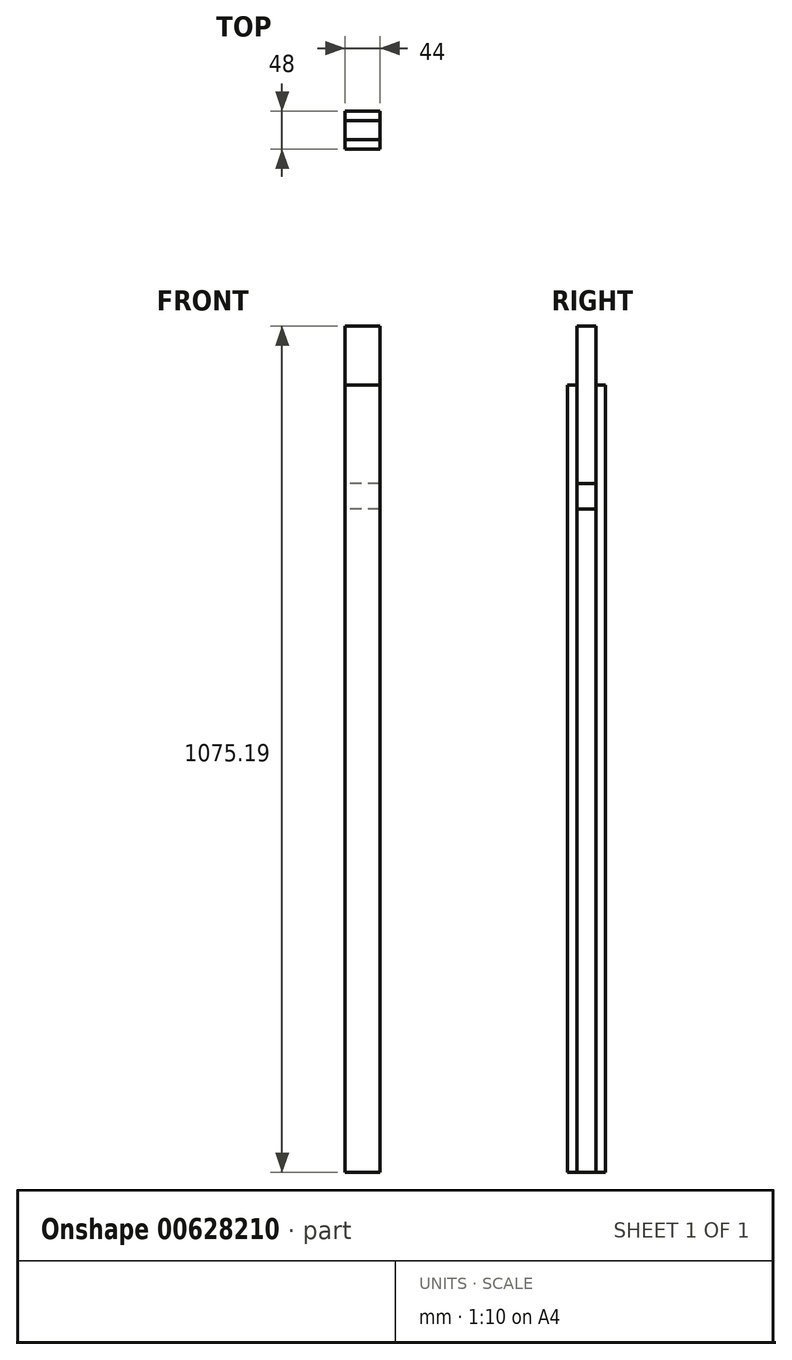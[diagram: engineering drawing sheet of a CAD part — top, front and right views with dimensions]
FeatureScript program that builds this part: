
annotation { "Feature Type Name" : "Feature", "Feature Type Description" : "" }
export const myFeature = defineFeature(function(context is Context, id is Id, definition is map)
    precondition{}
    {
        {
            var Q0;
            Q0=qCreatedBy(makeId("Right.planeOp"),FACE);
            var sketch = newSketch(context, id + "F0", { "sketchPlane" : qUnion([Q0])});
            skLineSegment(sketch, "E0", {"start": v(-12, 0) * mm, "end": v(12, 0) * mm});
            skLineSegment(sketch, "E1", {"start": v(-12, 0) * mm, "end": v(-12, 1000) * mm});
            skLineSegment(sketch, "E2", {"start": v(12, 1000) * mm, "end": v(12, 0) * mm});
            skLineSegment(sketch, "E3", {"start": v(-12, 1000) * mm, "end": v(-24, 1000) * mm});
            skLineSegment(sketch, "E4", {"start": v(-24, 1000) * mm, "end": v(-24, 0) * mm});
            skLineSegment(sketch, "E5", {"start": v(-24, 0) * mm, "end": v(-12, 0) * mm});
            skLineSegment(sketch, "E6", {"start": v(12, 1000) * mm, "end": v(24, 1000) * mm});
            skLineSegment(sketch, "E7", {"start": v(24, 1000) * mm, "end": v(24, 0) * mm});
            skLineSegment(sketch, "E8", {"start": v(24, 0) * mm, "end": v(12, 0) * mm});
            skLineSegment(sketch, "E9", {"start": v(-12, 1000) * mm, "end": v(-12, 1075.19) * mm});
            skLineSegment(sketch, "E10", {"start": v(-12, 1075.19) * mm, "end": v(12, 1075.19) * mm});
            skLineSegment(sketch, "E11", {"start": v(12, 1075.19) * mm, "end": v(12, 1000) * mm});
            skLineSegment(sketch, "E12", {"start": v(-12, 875.19) * mm, "end": v(12, 875.19) * mm});
            skLineSegment(sketch, "E13", {"start": v(-12, 842.84) * mm, "end": v(12, 842.84) * mm});
            skSolve(sketch);
        }
        {
            var Q0;
            {var subQ0=sQuery(id+"F0.wireOp",EDGE,"E3");Q0=makeQuery(id+"F0.imprint","IMPRINT",FACE,{"disambiguationData":[TD([[makeQuery(id+"F0.imprint","IMPRINT",EDGE,{"derivedFrom":subQ0}),1.0]])]});}
            var Q1;
            {var subQ3=sQuery(id+"F0.wireOp",EDGE,"E6");Q1=makeQuery(id+"F0.imprint","IMPRINT",FACE,{"disambiguationData":[TD([[makeQuery(id+"F0.imprint","IMPRINT",EDGE,{"derivedFrom":subQ3}),-1.0]])]});}
            extrude(context, id + "F1", {"entities" : qUnion([Q0, Q1]), "depth" : 44 * mm, "offsetDistance" : 25 * mm});
        }
        {
            var Q0;
            {var subQ0=sQuery(id+"F0.wireOp",EDGE,"E0");Q0=makeQuery(id+"F0.imprint","IMPRINT",FACE,{"disambiguationData":[TD([[makeQuery(id+"F0.imprint","IMPRINT",EDGE,{"derivedFrom":subQ0}),1.0]])]});}
            var Q1;
            {var subQ0=sQuery(id+"F0.wireOp",EDGE,"E9");Q1=makeQuery(id+"F0.imprint","IMPRINT",FACE,{"disambiguationData":[TD([[makeQuery(id+"F0.imprint","IMPRINT",EDGE,{"derivedFrom":subQ0}),-1.0]])]});}
            var Q2;
            Q2=makeQuery(id+"F1.opExtrude","CAP_FACE",FACE,{"disambiguationData":[OSD([sQuery(id+"F0.wireOp",EDGE,"E2"),sQuery(id+"F0.wireOp",EDGE,"E6"),sQuery(id+"F0.wireOp",EDGE,"E7"),sQuery(id+"F0.wireOp",EDGE,"E8")])],"isStart":false});
            extrude(context, id + "F2", {"entities" : qUnion([Q0, Q1]), "endBound" : BoundingType.UP_TO_SURFACE, "depth" : 25 * mm, "endBoundEntityFace" : qUnion([Q2]), "offsetDistance" : 25 * mm});
        }
    });
